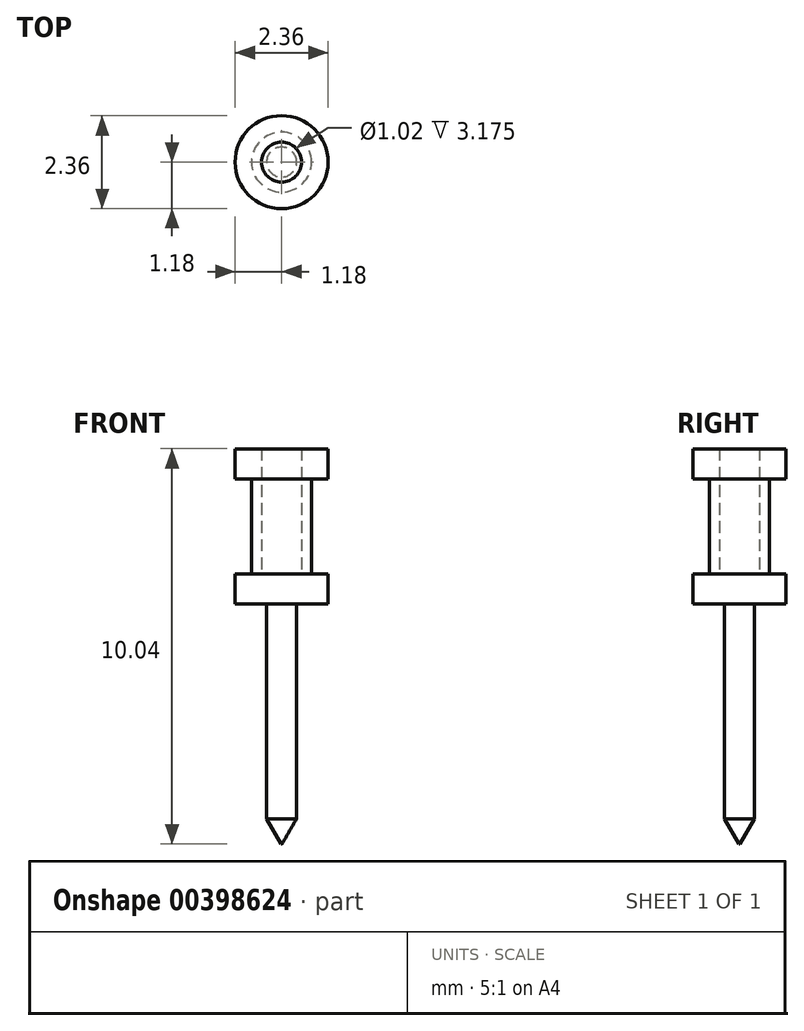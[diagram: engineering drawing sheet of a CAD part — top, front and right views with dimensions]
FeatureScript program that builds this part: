
annotation { "Feature Type Name" : "Feature", "Feature Type Description" : "" }
export const myFeature = defineFeature(function(context is Context, id is Id, definition is map)
    precondition{}
    {
        {
            var Q0;
            Q0=qCreatedBy(makeId("Top.planeOp"),FACE);
            var sketch = newSketch(context, id + "F0", { "sketchPlane" : qUnion([Q0])});
            skCircle(sketch, "E0", {"center": v(0, 0) * mm, "radius": 0.38 * mm});
            skCircle(sketch, "E1", {"center": v(0, 0) * mm, "radius": 1.18 * mm});
            skSolve(sketch);
        }
        {
            var Q0;
            Q0=makeQuery(id+"F0.imprint","IMPRINT",FACE,{"disambiguationData":[TD([[makeQuery(id+"F0.imprint","IMPRINT",EDGE,{"derivedFrom":sQuery(id+"F0.wireOp",EDGE,"E0")}),1.0]])]});
            extrude(context, id + "F1", {"entities" : qUnion([Q0]), "oppositeDirection" : true, "depth" : 6.1 * mm});
        }
        {
            var Q0;
            Q0=makeQuery(id+"F1.opExtrude","CAP_EDGE",EDGE,{"disambiguationData":[OSD([sQuery(id+"F0.wireOp",EDGE,"E0")])],"isStart":false});
            chamfer(context, id + "F2", {"entities" : qUnion([Q0]), "chamferType" : ChamferType.OFFSET_ANGLE, "width" : 0.64 * mm, "oppositeDirection" : false, "angle" : 30 * degree, "tangentPropagation" : true});
        }
        {
            var Q0;
            Q0 = qSketchRegion(id + "F0", true);
            var Q1;
            Q1=makeQuery(id+"F1.opExtrude","CAP_FACE",FACE,{"disambiguationData":[OSD([sQuery(id+"F0.wireOp",EDGE,"E0")])],"isStart":true});
            extrude(context, id + "F3", {"entities" : qUnion([Q0, Q1]), "operationType" : NewBodyOperationType.ADD, "depth" : 0.76 * mm});
        }
        {
            var Q0;
            {var subQ0=sQuery(id+"F0.wireOp",EDGE,"E0");Q0=makeQuery(id+"F3.boolean.opBoolean","MERGE",FACE,{"derivedFrom":[makeQuery(id+"F3.opExtrude","CAP_FACE",FACE,{"disambiguationData":[OSD([subQ0,sQuery(id+"F0.wireOp",EDGE,"E1")])],"isStart":false}),makeQuery(id+"F3.opExtrude","CAP_FACE",FACE,{"disambiguationData":[OSD([subQ0])],"isStart":false})]});}
            var sketch = newSketch(context, id + "F4", { "sketchPlane" : qUnion([Q0])});
            skCircle(sketch, "E2", {"center": v(0, 0) * mm, "radius": 0.76 * mm});
            skCircle(sketch, "E3", {"center": v(0, 0) * mm, "radius": 0.5 * mm});
            skSolve(sketch);
        }
        {
            var Q0;
            Q0=makeQuery(id+"F4.imprint","IMPRINT",FACE,{"disambiguationData":[TD([[makeQuery(id+"F4.imprint","IMPRINT",EDGE,{"derivedFrom":sQuery(id+"F4.wireOp",EDGE,"E2")}),1.0]])]});
            extrude(context, id + "F5", {"entities" : qUnion([Q0]), "operationType" : NewBodyOperationType.ADD, "depth" : 2.41 * mm});
        }
        {
            var Q0;
            Q0=makeQuery(id+"F5.opExtrude","CAP_FACE",FACE,{"disambiguationData":[OSD([sQuery(id+"F4.wireOp",EDGE,"E2"),sQuery(id+"F4.wireOp",EDGE,"E3")])],"isStart":false});
            var sketch = newSketch(context, id + "F6", { "sketchPlane" : qUnion([Q0])});
            skCircle(sketch, "E4", {"center": v(0, 0) * mm, "radius": 1.18 * mm});
            skCircle(sketch, "E5", {"center": v(0, 0) * mm, "radius": 0.5 * mm});
            skSolve(sketch);
        }
        {
            var Q0;
            Q0=makeQuery(id+"F6.imprint","IMPRINT",FACE,{"disambiguationData":[TD([[makeQuery(id+"F6.imprint","IMPRINT",EDGE,{"derivedFrom":sQuery(id+"F6.wireOp",EDGE,"E4")}),1.0]])]});
            var Q1;
            Q1=makeQuery(id+"F6.imprint","IMPRINT",FACE,{"disambiguationData":[TD([[makeQuery(id+"F6.imprint","IMPRINT",EDGE,{"derivedFrom":sQuery(id+"F6.wireOp",EDGE,"E5")}),-1.0]])]});
            extrude(context, id + "F7", {"entities" : qUnion([Q0, Q1]), "operationType" : NewBodyOperationType.ADD, "depth" : 0.76 * mm});
        }
    });
